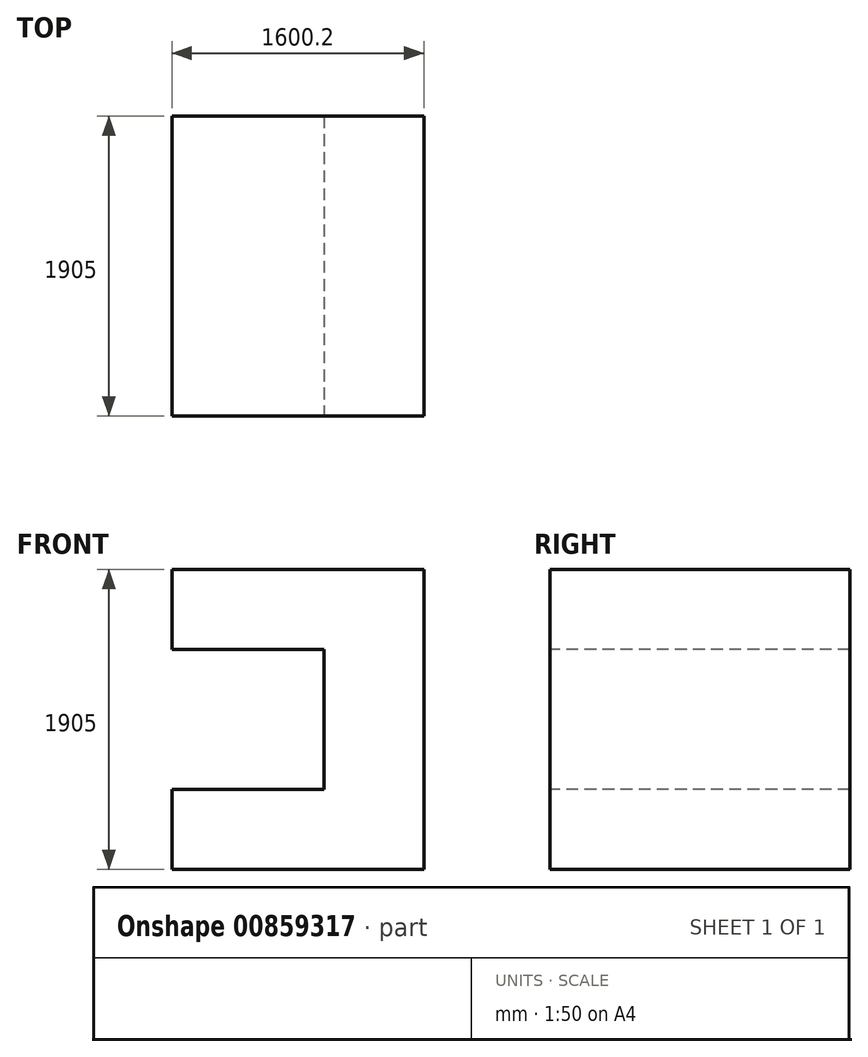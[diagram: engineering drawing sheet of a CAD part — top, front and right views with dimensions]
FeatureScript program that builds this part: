
annotation { "Feature Type Name" : "Feature", "Feature Type Description" : "" }
export const myFeature = defineFeature(function(context is Context, id is Id, definition is map)
    precondition{}
    {
        {
            var Q0;
            Q0=qCreatedBy(makeId("Front.planeOp"),FACE);
            var sketch = newSketch(context, id + "F0", { "sketchPlane" : qUnion([Q0])});
            skLineSegment(sketch, "E0", {"start": v(0, 0) * mm, "end": v(1600.2, 0) * mm});
            skLineSegment(sketch, "E1", {"start": v(1600.2, 0) * mm, "end": v(1600.2, 1905) * mm});
            skLineSegment(sketch, "E2", {"start": v(1600.2, 1905) * mm, "end": v(0, 1905) * mm});
            skLineSegment(sketch, "E3", {"start": v(0, 1905) * mm, "end": v(0, 1397) * mm});
            skLineSegment(sketch, "E4", {"start": v(0, 1397) * mm, "end": v(965.2, 1397) * mm});
            skLineSegment(sketch, "E5", {"start": v(965.2, 1397) * mm, "end": v(965.2, 508) * mm});
            skLineSegment(sketch, "E6", {"start": v(965.2, 508) * mm, "end": v(0, 508) * mm});
            skLineSegment(sketch, "E7", {"start": v(0, 508) * mm, "end": v(0, 0) * mm});
            skSolve(sketch);
        }
        {
            var Q0;
            Q0 = qSketchRegion(id + "F0", true);
            extrude(context, id + "F1", {"entities" : qUnion([Q0]), "oppositeDirection" : true, "depth" : 1905 * mm, "offsetDistance" : 25.4 * mm});
        }
    });
